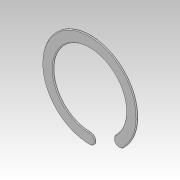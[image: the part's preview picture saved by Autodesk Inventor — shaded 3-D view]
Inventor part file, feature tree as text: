
AUTODESK INVENTOR PART (.ipt)
format: ipt  version: 2020 (Build 240168000, 168)  size: 167,936 bytes
history: native  units: mm
features: projected_geometry x9, other x3, extrude x3, sketch x3, fillet x1
ambient origin geometry x8: Origin, YZ Plane, XZ Plane, XY Plane, X Axis, Y Axis, Z Axis, Center Point
bodies: Solid1 (feature_tree)
feature tree (19):
  other  "Blocks"
  extrude  "Extrusion1"  Depth=0.15mm
  extrude  "Extrusion2"  Depth=80.0mm TaperAngle=360.0deg
  fillet  "Fillet1"  Radius=0.2mm
  extrude  "Extrusion3"  Depth=0.5mm
  sketch  "Sketch1"  dims[d0=8.0mm d1=0.15mm]
  other  "Block1"
  sketch  "Sketch2"  dims[d2=5.8mm d3=80.0mm d5=360.0deg d7=0.2mm d8=0.0mm]
  projected_geometry  "Projected Loop1"
  sketch  "Sketch3"  dims[d9=0.6mm d10=0.0mm d11=0.5mm d12=10.0mm d13=0.0mm]
  projected_geometry  "Projected Loop2"
  projected_geometry  "Projected Loop3"
  projected_geometry  "Projected Loop4"
  projected_geometry  "Projected Loop5"
  projected_geometry  "Projected Loop6"
  projected_geometry  "Projected Loop7"
  projected_geometry  "Projected Loop8"
  projected_geometry  "Projected Loop9"
  other  "Block1:1"
